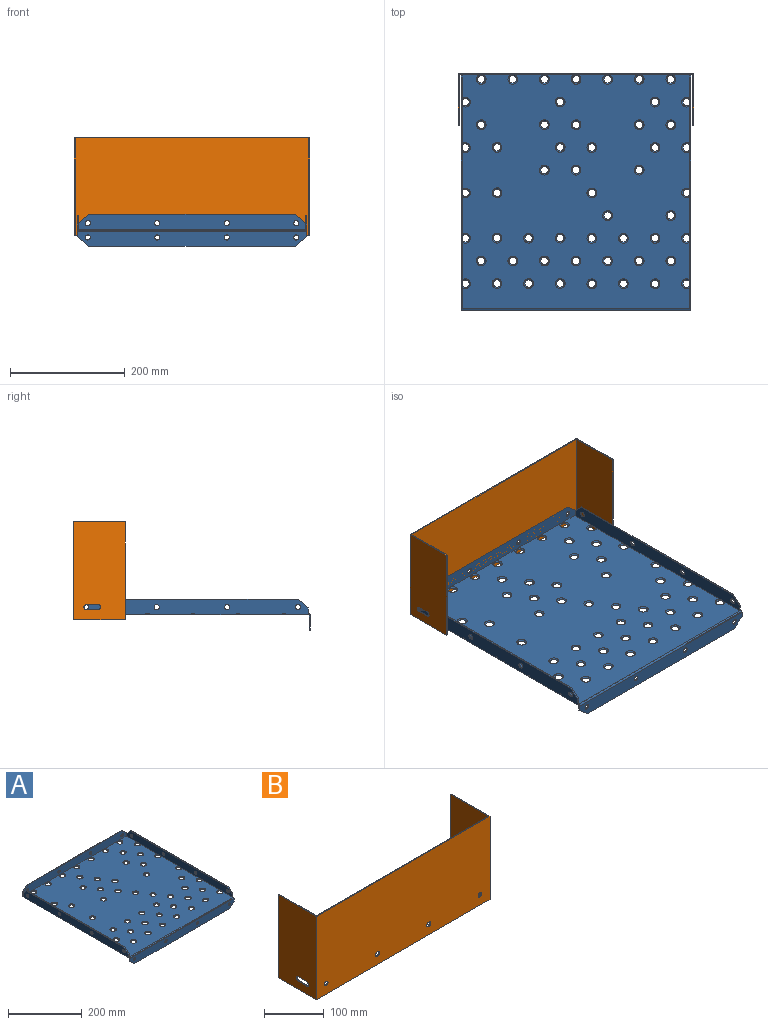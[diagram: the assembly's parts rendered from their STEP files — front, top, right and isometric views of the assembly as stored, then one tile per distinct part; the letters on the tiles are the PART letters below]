
ASSEMBLY  parts=2 mates=1
PART A: 117 faces, bbox 400x412x55.2 mm
  f0: plane 412x37mm, normal (-1,0,0), area 10471.9mm2, adj f1,f9,f10,f11,f12,f13,f28,f30
  f1: plane 20x16.61mm, normal (-0.64,0,-0.77), area 52mm2, adj f0,f2,f9,f10
  f2: plane 360x2mm, normal (0,0,-1), area 720mm2, adj f1,f3,f9,f10
  f3: plane 20x16.61mm, normal (0.64,0,-0.77), area 52mm2, adj f2,f8,f9,f10
  f4: cylinder r=4.5mm len=9mm, axis (0,-1,0), area 56.5mm2, adj f9,f10
  f5: cylinder r=4.5mm len=9mm, axis (0,-1,0), area 56.5mm2, adj f9,f10
  f6: cylinder r=4.5mm len=9mm, axis (0,-1,0), area 56.5mm2, adj f9,f10
  f7: cylinder r=4.5mm len=9mm, axis (0,-1,0), area 56.5mm2, adj f9,f10
  f8: plane 412x37mm, normal (1,0,0), area 10471.9mm2, adj f3,f9,f10,f11,f12,f13,f43,f45
  f9: plane 400x26.61mm, normal (0,1,0), area 10058.6mm2, adj f0,f1,f2,f3,f4,f5,f6,f7
  f10: plane 400x25.61mm, normal (0,-1,0), area 9658.6mm2, adj f0,f1,f2,f3,f4,f5,f6,f7
  f11: plane 410x400mm, normal (0,0,-1), area 156832.5mm2, adj f0,f8,f9,f13,f14,f15,f16,f17
  f12: plane 407x400mm, normal (0,0,1), area 149217.5mm2, adj f0,f8,f28,f30,f38,f43,f45,f53
  f13: plane 400x28.61mm, normal (0,1,0), area 10858.6mm2, adj f0,f8,f11,f54,f55,f56,f57,f58
  f14: cylinder r=6.5mm len=6.93mm, axis (0,0,-1), area 14.6mm2, adj f11,f29,f38
  f15: cylinder r=6.5mm len=6.93mm, axis (0,0,-1), area 14.6mm2, adj f11,f44,f53
  f16: cylinder r=6.5mm len=6.93mm, axis (0,0,-1), area 14.6mm2, adj f11,f42,f53
  f17: cylinder r=6.5mm len=6.93mm, axis (0,0,-1), area 14.6mm2, adj f11,f27,f38
  f18: cylinder r=6.5mm len=6.93mm, axis (0,0,-1), area 14.6mm2, adj f11,f41,f53
  f19: cylinder r=6.5mm len=6.93mm, axis (0,0,-1), area 14.6mm2, adj f11,f26,f38
  f20: cylinder r=6.5mm len=6.93mm, axis (0,0,-1), area 14.6mm2, adj f11,f40,f53
  f21: cylinder r=6.5mm len=6.93mm, axis (0,0,-1), area 14.6mm2, adj f11,f25,f38
  f22: cylinder r=6.5mm len=6.93mm, axis (0,0,-1), area 14.6mm2, adj f11,f39,f53
  f23: cylinder r=6.5mm len=6.93mm, axis (0,0,-1), area 14.6mm2, adj f11,f24,f38
  f24: plane 6.93x1mm, normal (0,0,-1), area 4.7mm2, adj f23,f38
  f25: plane 6.93x1mm, normal (0,0,-1), area 4.7mm2, adj f21,f38
  f26: plane 6.93x1mm, normal (0,0,-1), area 4.7mm2, adj f19,f38
  f27: plane 6.93x1mm, normal (0,0,-1), area 4.7mm2, adj f17,f38
  f28: plane 10x2mm, normal (0,-1,0), area 20mm2, adj f0,f12,f36,f38
  f29: plane 6.93x1mm, normal (0,0,-1), area 4.7mm2, adj f14,f38
  f30: plane 10x2mm, normal (0,1,0), area 20mm2, adj f0,f12,f31,f38
  f31: plane 15x13.93mm, normal (0,0.73,0.68), area 40.9mm2, adj f0,f30,f32,f38
  f32: plane 372.57x2mm, normal (0,0,1), area 745.1mm2, adj f0,f31,f36,f38
  f33: cylinder r=4.5mm len=9mm, axis (1,0,0), area 56.5mm2, adj f0,f38
  f34: cylinder r=4.5mm len=9mm, axis (1,0,0), area 56.5mm2, adj f0,f38
  f35: cylinder r=4.5mm len=9mm, axis (1,0,0), area 56.5mm2, adj f0,f38
  f36: plane 17.5x15mm, normal (0,-0.65,0.76), area 46.1mm2, adj f0,f28,f32,f38
  f37: cylinder r=4.5mm len=9mm, axis (1,0,0), area 56.5mm2, adj f0,f38
  f38: plane 404x27mm, normal (1,0,0), area 9641.7mm2, adj f12,f14,f17,f19,f21,f23,f24,f25
  f39: plane 6.93x1mm, normal (0,0,-1), area 4.7mm2, adj f22,f53
  f40: plane 6.93x1mm, normal (0,0,-1), area 4.7mm2, adj f20,f53
  f41: plane 6.93x1mm, normal (0,0,-1), area 4.7mm2, adj f18,f53
  f42: plane 6.93x1mm, normal (0,0,-1), area 4.7mm2, adj f16,f53
  f43: plane 10x2mm, normal (0,-1,0), area 20mm2, adj f8,f12,f51,f53
  f44: plane 6.93x1mm, normal (0,0,-1), area 4.7mm2, adj f15,f53
  f45: plane 10x2mm, normal (0,1,0), area 20mm2, adj f8,f12,f46,f53
  f46: plane 15x13.93mm, normal (0,0.73,0.68), area 40.9mm2, adj f8,f45,f47,f53
  f47: plane 372.57x2mm, normal (0,0,1), area 745.1mm2, adj f8,f46,f51,f53
  f48: cylinder r=4.5mm len=9mm, axis (1,0,0), area 56.5mm2, adj f8,f53
  f49: cylinder r=4.5mm len=9mm, axis (1,0,0), area 56.5mm2, adj f8,f53
  f50: cylinder r=4.5mm len=9mm, axis (1,0,0), area 56.5mm2, adj f8,f53
  f51: plane 17.5x15mm, normal (0,-0.65,0.76), area 46.1mm2, adj f8,f43,f47,f53
  f52: cylinder r=4.5mm len=9mm, axis (1,0,0), area 56.5mm2, adj f8,f53
  f53: plane 404x27mm, normal (-1,0,0), area 9641.7mm2, adj f12,f15,f16,f18,f20,f22,f39,f40
  f54: plane 20x16.61mm, normal (-0.64,0,0.77), area 52mm2, adj f0,f13,f55,f61
  f55: plane 360x2mm, normal (0,0,1), area 720mm2, adj f13,f54,f56,f61
  f56: plane 20x16.61mm, normal (0.64,0,0.77), area 52mm2, adj f8,f13,f55,f61
  f57: cylinder r=4.5mm len=9mm, axis (0,1,0), area 56.5mm2, adj f13,f61
  f58: cylinder r=4.5mm len=9mm, axis (0,1,0), area 56.5mm2, adj f13,f61
  f59: cylinder r=4.5mm len=9mm, axis (0,1,0), area 56.5mm2, adj f13,f61
  f60: cylinder r=4.5mm len=9mm, axis (0,1,0), area 56.5mm2, adj f13,f61
  f61: plane 400x27.28mm, normal (0,-1,0), area 10078.7mm2, adj f0,f8,f12,f54,f55,f56,f57,f58
  f62: cone r=6.5mm half-angle=45deg, axis (0,0,1), area 133.3mm2, adj f11,f12
  f63: cone r=6.5mm half-angle=45deg, axis (0,0,1), area 133.3mm2, adj f11,f12
  f64: cone r=6.5mm half-angle=45deg, axis (0,0,1), area 101.7mm2, adj f11,f12,f38
  f65: cone r=6.5mm half-angle=45deg, axis (0,0,1), area 133.3mm2, adj f11,f12
  f66: cone r=6.5mm half-angle=45deg, axis (0,0,1), area 133.3mm2, adj f11,f12
  f67: cone r=6.5mm half-angle=45deg, axis (0,0,1), area 133.3mm2, adj f11,f12
  f68: cone r=6.5mm half-angle=45deg, axis (0,0,1), area 133.3mm2, adj f11,f12
  f69: cone r=6.5mm half-angle=45deg, axis (0,0,1), area 133.3mm2, adj f11,f12
  f70: cone r=6.5mm half-angle=45deg, axis (0,0,1), area 133.3mm2, adj f11,f12
  f71: cone r=6.5mm half-angle=45deg, axis (0,0,1), area 101.7mm2, adj f11,f12,f38
  f72: cone r=6.5mm half-angle=45deg, axis (0,0,1), area 101.7mm2, adj f11,f12,f38
  f73: cone r=6.5mm half-angle=45deg, axis (0,0,1), area 101.7mm2, adj f11,f12,f38
  f74: cone r=6.5mm half-angle=45deg, axis (0,0,1), area 101.7mm2, adj f11,f12,f38
  f75: cone r=6.5mm half-angle=45deg, axis (0,0,1), area 133.3mm2, adj f11,f12
  f76: cone r=6.5mm half-angle=45deg, axis (0,0,1), area 133.3mm2, adj f11,f12
  f77: cone r=6.5mm half-angle=45deg, axis (0,0,1), area 133.3mm2, adj f11,f12
  f78: cone r=6.5mm half-angle=45deg, axis (0,0,1), area 133.3mm2, adj f11,f12
  f79: cone r=6.5mm half-angle=45deg, axis (0,0,1), area 133.3mm2, adj f11,f12
  f80: cone r=6.5mm half-angle=45deg, axis (0,0,1), area 133.3mm2, adj f11,f12
  f81: cone r=6.5mm half-angle=45deg, axis (0,0,1), area 133.3mm2, adj f11,f12
  f82: cone r=6.5mm half-angle=45deg, axis (0,0,1), area 133.3mm2, adj f11,f12
  f83: cone r=6.5mm half-angle=45deg, axis (0,0,1), area 133.3mm2, adj f11,f12
  f84: cone r=6.5mm half-angle=45deg, axis (0,0,1), area 101.7mm2, adj f11,f12,f53
  f85: cone r=6.5mm half-angle=45deg, axis (0,0,1), area 133.3mm2, adj f11,f12
  f86: cone r=6.5mm half-angle=45deg, axis (0,0,1), area 133.3mm2, adj f11,f12
  f87: cone r=6.5mm half-angle=45deg, axis (0,0,1), area 133.3mm2, adj f11,f12
  f88: cone r=6.5mm half-angle=45deg, axis (0,0,1), area 129.2mm2, adj f11,f12,f61
  f89: cone r=6.5mm half-angle=45deg, axis (0,0,1), area 129.2mm2, adj f11,f12,f61
  f90: cone r=6.5mm half-angle=45deg, axis (0,0,1), area 129.2mm2, adj f11,f12,f61
  f91: cone r=6.5mm half-angle=45deg, axis (0,0,1), area 129.2mm2, adj f11,f12,f61
  f92: cone r=6.5mm half-angle=45deg, axis (0,0,1), area 129.2mm2, adj f11,f12,f61
  f93: cone r=6.5mm half-angle=45deg, axis (0,0,1), area 133.3mm2, adj f11,f12
  f94: cone r=6.5mm half-angle=45deg, axis (0,0,1), area 133.3mm2, adj f11,f12
  f95: cone r=6.5mm half-angle=45deg, axis (0,0,1), area 133.3mm2, adj f11,f12
  f96: cone r=6.5mm half-angle=45deg, axis (0,0,1), area 133.3mm2, adj f11,f12
  f97: cone r=6.5mm half-angle=45deg, axis (0,0,1), area 129.2mm2, adj f11,f12,f61
  f98: cone r=6.5mm half-angle=45deg, axis (0,0,1), area 129.2mm2, adj f11,f12,f61
  f99: cone r=6.5mm half-angle=45deg, axis (0,0,1), area 101.7mm2, adj f11,f12,f53
  f100: cone r=6.5mm half-angle=45deg, axis (0,0,1), area 101.7mm2, adj f11,f12,f53
  f101: cone r=6.5mm half-angle=45deg, axis (0,0,1), area 133.3mm2, adj f11,f12
  f102: cone r=6.5mm half-angle=45deg, axis (0,0,1), area 101.7mm2, adj f11,f12,f53
  f103: cone r=6.5mm half-angle=45deg, axis (0,0,1), area 101.7mm2, adj f11,f12,f53
  f104: cone r=6.5mm half-angle=45deg, axis (0,0,1), area 133.3mm2, adj f11,f12
  f105: cone r=6.5mm half-angle=45deg, axis (0,0,1), area 133.3mm2, adj f11,f12
  f106: cone r=6.5mm half-angle=45deg, axis (0,0,1), area 133.3mm2, adj f11,f12
  f107: cone r=6.5mm half-angle=45deg, axis (0,0,1), area 133.3mm2, adj f11,f12
  f108: cone r=6.5mm half-angle=45deg, axis (0,0,1), area 133.3mm2, adj f11,f12
  f109: cone r=6.5mm half-angle=45deg, axis (0,0,1), area 133.3mm2, adj f11,f12
  f110: cone r=6.5mm half-angle=45deg, axis (0,0,1), area 133.3mm2, adj f11,f12
  f111: cone r=6.5mm half-angle=45deg, axis (0,0,1), area 133.3mm2, adj f11,f12
  f112: cone r=6.5mm half-angle=45deg, axis (0,0,1), area 133.3mm2, adj f11,f12
  f113: cone r=6.5mm half-angle=45deg, axis (0,0,1), area 133.3mm2, adj f11,f12
  f114: cone r=6.5mm half-angle=45deg, axis (0,0,1), area 133.3mm2, adj f11,f12
  f115: cone r=6.5mm half-angle=45deg, axis (0,0,1), area 133.3mm2, adj f11,f12
  f116: cylinder r=3mm len=400mm, axis (-1,0,0), area 1885mm2, adj f0,f8,f10,f12
PART B: 22 faces, bbox 410x90x170 mm
  f0: plane 170x90mm, normal (-1,0,0), area 15058.6mm2, adj f1,f7,f8,f9,f14,f15,f16,f17
  f1: plane 410x170mm, normal (0,-1,0), area 69445.5mm2, adj f0,f2,f8,f9,f10,f11,f12,f13
  f2: plane 170x90mm, normal (1,0,0), area 15058.6mm2, adj f1,f3,f8,f9,f18,f19,f20,f21
  f3: plane 170x2mm, normal (0,1,0), area 340mm2, adj f2,f4,f8,f9
  f4: plane 170x88mm, normal (-1,0,0), area 14718.6mm2, adj f3,f5,f8,f9,f18,f19,f20,f21
  f5: plane 406x170mm, normal (0,1,0), area 68765.5mm2, adj f4,f6,f8,f9,f10,f11,f12,f13
  f6: plane 170x88mm, normal (1,0,0), area 14718.6mm2, adj f5,f7,f8,f9,f14,f15,f16,f17
  f7: plane 170x2mm, normal (0,1,0), area 340mm2, adj f0,f6,f8,f9
  f8: plane 410x90mm, normal (0,0,1), area 1172mm2, adj f0,f1,f2,f3,f4,f5,f6,f7
  f9: plane 410x90mm, normal (0,0,-1), area 1172mm2, adj f0,f1,f2,f3,f4,f5,f6,f7
  f10: cylinder r=4.5mm len=9mm, axis (0,-1,0), area 56.5mm2, adj f1,f5
  f11: cylinder r=4.5mm len=9mm, axis (0,-1,0), area 56.5mm2, adj f1,f5
  f12: cylinder r=4.5mm len=9mm, axis (0,-1,0), area 56.5mm2, adj f1,f5
  f13: cylinder r=4.5mm len=9mm, axis (0,-1,0), area 56.5mm2, adj f1,f5
  f14: plane 19.53x2mm, normal (0,0,-1), area 39.1mm2, adj f0,f6,f15,f17
  f15: cylinder r=4.5mm len=9mm, axis (1,0,0), area 28.3mm2, adj f0,f6,f14,f16
  f16: plane 19.77x2mm, normal (0,0,1), area 39.5mm2, adj f0,f6,f15,f17
  f17: cylinder r=4.5mm len=9mm, axis (1,0,0), area 28.7mm2, adj f0,f6,f14,f16
  f18: cylinder r=4.5mm len=9mm, axis (1,0,0), area 28.7mm2, adj f2,f4,f19,f21
  f19: plane 19.77x2mm, normal (0,0,1), area 39.5mm2, adj f2,f4,f18,f20
  f20: cylinder r=4.5mm len=9mm, axis (1,0,0), area 28.3mm2, adj f2,f4,f19,f21
  f21: plane 19.53x2mm, normal (0,0,-1), area 39.1mm2, adj f2,f4,f18,f20
PLACE A t=(15.14,-2.59,-16.49)mm
PLACE B rot(axis=(0,0,1),180deg) t=(220.09,203.41,-24.67)mm
MATE planar B.f11 <-> A.f57  axis (0,-1,0) through (-166.41,201.41,-3.17)mm
